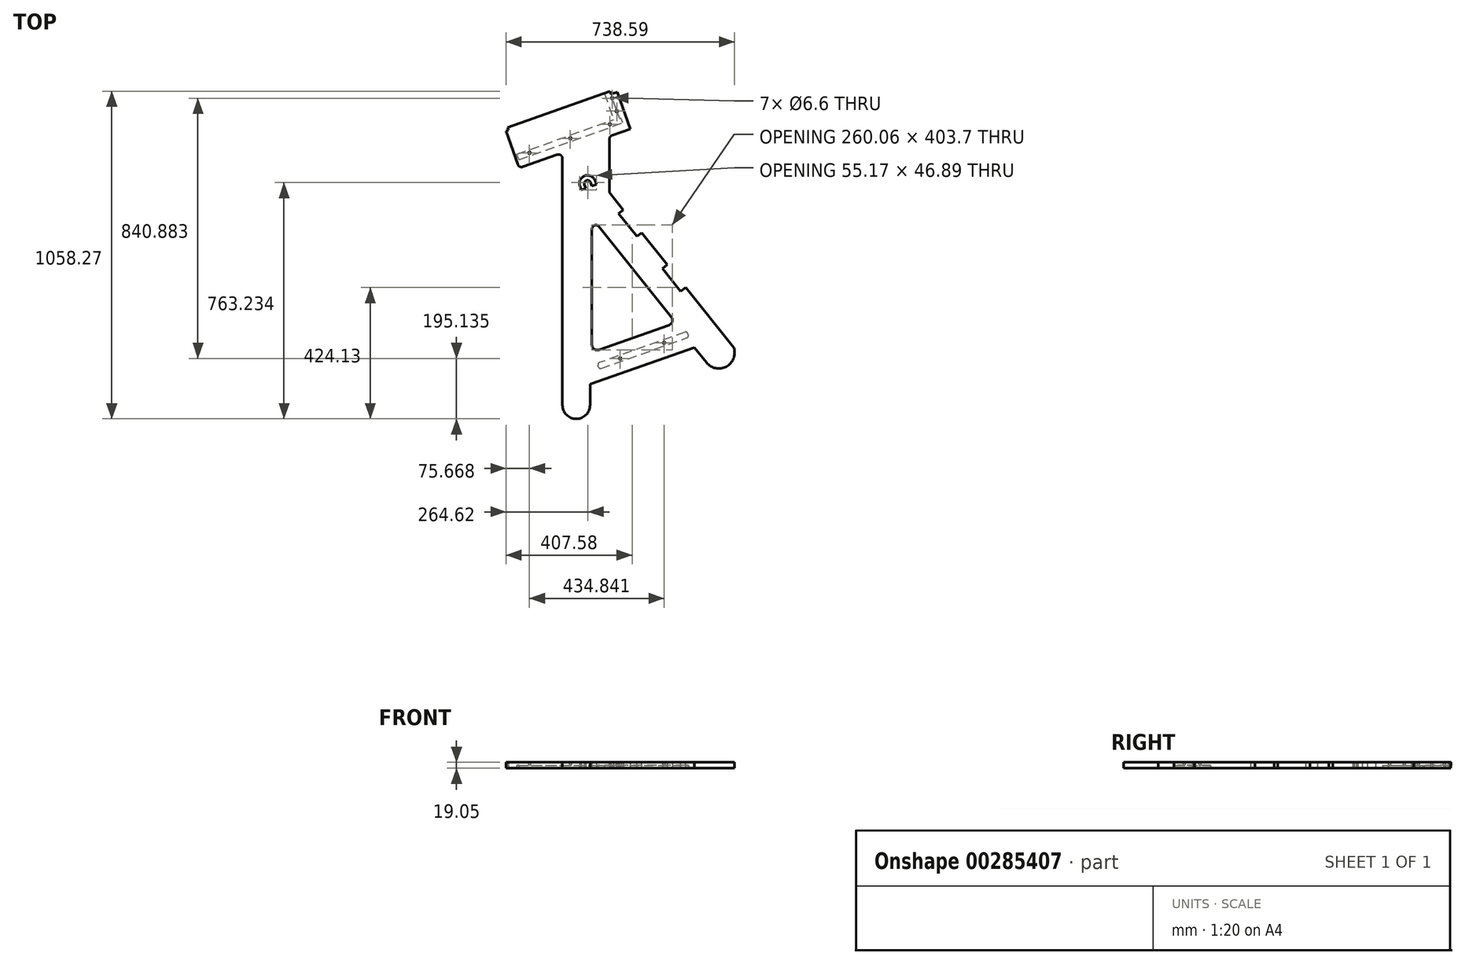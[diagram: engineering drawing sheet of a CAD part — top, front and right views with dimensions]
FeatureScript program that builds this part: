
annotation { "Feature Type Name" : "Feature", "Feature Type Description" : "" }
export const myFeature = defineFeature(function(context is Context, id is Id, definition is map)
    precondition{}
    {
        {
            var Q0;
            Q0=qCreatedBy(makeId("Top.planeOp"),FACE);
            var sketch = newSketch(context, id + "F0", { "sketchPlane" : qUnion([Q0])});
            skLineSegment(sketch, "E0", {"start": v(-306.62, -10.3) * mm, "end": v(-306.88, -10.27) * mm});
            skLineSegment(sketch, "E1", {"start": v(727.27, -289.32) * mm, "end": v(727.27, 507.63) * mm});
            skPoint(sketch, "E2.visualSharp", {"position": v(727.27, -334.1) * mm});
            skPoint(sketch, "E3.visualSharp", {"position": v(828.87, -334.66) * mm});
            skLineSegment(sketch, "E4", {"start": v(878.9, 569.94) * mm, "end": v(878.9, 402.04) * mm});
            skLineSegment(sketch, "E5", {"start": v(710.35, 519.6) * mm, "end": v(599.11, 480.45) * mm});
            skLineSegment(sketch, "E6", {"start": v(582.92, 488.22) * mm, "end": v(544.97, 596.03) * mm});
            skLineSegment(sketch, "E7", {"start": v(544.97, 596.03) * mm, "end": v(552.9, 598.83) * mm});
            skLineSegment(sketch, "E8", {"start": v(904.35, 722.53) * mm, "end": v(946.52, 602.74) * mm});
            skLineSegment(sketch, "E9", {"start": v(887.38, 581.92) * mm, "end": v(946.52, 602.74) * mm});
            skLineSegment(sketch, "E10", {"start": v(822.52, -95.2) * mm, "end": v(822.52, 279.38) * mm});
            skLineSegment(sketch, "E11", {"start": v(845.13, 287.31) * mm, "end": v(1078.98, -4.96) * mm});
            skPoint(sketch, "E12.visualSharp", {"position": v(822.52, 315.58) * mm});
            skArc(sketch, "E12.filletArc", {"start": v(845.13, 287.31) * mm, "mid": v(831.01, 291.36) * mm, "end": v(822.52, 279.38) * mm});
            skLineSegment(sketch, "E13", {"start": v(587.13, 476.24) * mm, "end": v(946.52, 602.74) * mm, "construction": true});
            skLineSegment(sketch, "E14", {"start": v(881.68, 394.1) * mm, "end": v(1281.26, -105.33) * mm});
            skArc(sketch, "E15", {"start": v(1192.97, -152.23) * mm, "mid": v(1256.56, -165.38) * mm, "end": v(1281.26, -105.33) * mm});
            skLineSegment(sketch, "E16", {"start": v(816.46, -289.32) * mm, "end": v(816.46, -221.63) * mm});
            skLineSegment(sketch, "E17", {"start": v(926.55, 733.52) * mm, "end": v(1268.68, -238.42) * mm, "construction": true});
            skPoint(sketch, "E18.visualSharp", {"position": v(878.9, 397.58) * mm});
            skArc(sketch, "E18.filletArc", {"start": v(878.9, 402.04) * mm, "mid": v(879.61, 397.83) * mm, "end": v(881.68, 394.1) * mm});
            skPoint(sketch, "E19.visualSharp", {"position": v(878.9, 578.94) * mm});
            skArc(sketch, "E19.filletArc", {"start": v(887.38, 581.92) * mm, "mid": v(881.23, 577.28) * mm, "end": v(878.9, 569.94) * mm});
            skArc(sketch, "E20.filletArc", {"start": v(727.27, 507.63) * mm, "mid": v(721.9, 518) * mm, "end": v(710.35, 519.6) * mm});
            skLineSegment(sketch, "E21", {"start": v(549.74, 607.81) * mm, "end": v(880.86, 724.36) * mm});
            skLineSegment(sketch, "E22", {"start": v(549.74, 607.81) * mm, "end": v(552.9, 598.83) * mm});
            skLineSegment(sketch, "E23", {"start": v(880.86, 724.36) * mm, "end": v(884.02, 715.38) * mm});
            skLineSegment(sketch, "E24.trimOffspring", {"start": v(884.02, 715.38) * mm, "end": v(904.35, 722.53) * mm, "construction": true});
            skLineSegment(sketch, "E25.trimOffspring", {"start": v(884.02, 715.38) * mm, "end": v(904.35, 722.53) * mm});
            skLineSegment(sketch, "E26", {"start": v(544.97, 596.03) * mm, "end": v(903.18, -421.63) * mm, "construction": true});
            skLineSegment(sketch, "E27", {"start": v(869.21, -325.12) * mm, "end": v(1232.7, -197.18) * mm, "construction": true});
            skLineSegment(sketch, "E28", {"start": v(816.46, -221.63) * mm, "end": v(1153.56, -102.97) * mm});
            skLineSegment(sketch, "E29", {"start": v(844.5, -110.78) * mm, "end": v(1071.57, -30.85) * mm});
            skArc(sketch, "E30", {"start": v(727.27, -289.32) * mm, "mid": v(771.86, -333.91) * mm, "end": v(816.46, -289.32) * mm});
            skPoint(sketch, "E31.visualSharp", {"position": v(587.13, 476.24) * mm});
            skArc(sketch, "E31.filletArc", {"start": v(582.92, 488.22) * mm, "mid": v(589.4, 480.98) * mm, "end": v(599.11, 480.45) * mm});
            skPoint(sketch, "E32.visualSharp", {"position": v(1093.5, -23.13) * mm});
            skArc(sketch, "E32.filletArc", {"start": v(1071.57, -30.85) * mm, "mid": v(1081.96, -19.82) * mm, "end": v(1078.98, -4.96) * mm});
            skPoint(sketch, "E33.visualSharp", {"position": v(822.52, -118.52) * mm});
            skArc(sketch, "E33.filletArc", {"start": v(822.52, -95.2) * mm, "mid": v(829.49, -108.68) * mm, "end": v(844.5, -110.78) * mm});
            skLineSegment(sketch, "E34", {"start": v(1153.56, -102.97) * mm, "end": v(1192.97, -152.23) * mm});
            skPoint(sketch, "E35", {"position": v(1256.56, -165.38) * mm});
            skPoint(sketch, "E36", {"position": v(771.86, -333.91) * mm});
            skPoint(sketch, "E37", {"position": v(1272.05, -152.68) * mm});
            skLineSegment(sketch, "E38", {"start": v(786.67, -331.38) * mm, "end": v(1249.58, -168.44) * mm, "construction": true});
            skArc(sketch, "E39", {"start": v(817.98, 430.01) * mm, "mid": v(804.77, 436.34) * mm, "end": v(798.43, 423.13) * mm});
            skArc(sketch, "E40", {"start": v(832.96, 435.28) * mm, "mid": v(799.5, 451.32) * mm, "end": v(783.46, 417.86) * mm});
            skLineSegment(sketch, "E41", {"start": v(783.46, 417.86) * mm, "end": v(787.67, 405.88) * mm});
            skLineSegment(sketch, "E42", {"start": v(787.67, 405.88) * mm, "end": v(802.65, 411.15) * mm});
            skLineSegment(sketch, "E43", {"start": v(802.65, 411.15) * mm, "end": v(798.43, 423.13) * mm});
            skLineSegment(sketch, "E44", {"start": v(817.98, 430.01) * mm, "end": v(822.2, 418.03) * mm});
            skLineSegment(sketch, "E45", {"start": v(822.2, 418.03) * mm, "end": v(837.17, 423.3) * mm});
            skLineSegment(sketch, "E46", {"start": v(837.17, 423.3) * mm, "end": v(832.96, 435.28) * mm});
            skSolve(sketch);
        }
        {
            var Q0;
            Q0=makeQuery(id+"F0.imprint","IMPRINT",FACE,{"disambiguationData":[TD([[makeQuery(id+"F0.imprint","IMPRINT",EDGE,{"derivedFrom":sQuery(id+"F0.wireOp",EDGE,"oAVC5DI8-kh1G-Qbfy-uwvq-Txyh6lFHP0Ui")}),1.0]])]});
            var Q1;
            Q1=makeQuery(id+"F0.imprint","IMPRINT",FACE,{"disambiguationData":[TD([[makeQuery(id+"F0.imprint","IMPRINT",EDGE,{"derivedFrom":sQuery(id+"F0.wireOp",EDGE,"E1")}),-1.0]])]});
            extrude(context, id + "F1", {"entities" : qUnion([Q0, Q1]), "depth" : 19.05 * mm});
        }
        {
            var Q0;
            {var subQ2=sQuery(id+"F0.wireOp",EDGE,"E1");Q0=makeQuery(id+"F0.imprint","IMPRINT",FACE,{"disambiguationData":[TD([[makeQuery(id+"F0.imprint","IMPRINT",EDGE,{"derivedFrom":subQ2}),-1.0]])]});}
            var sketch = newSketch(context, id + "F2", { "sketchPlane" : qUnion([Q0])});
            skLineSegment(sketch, "E47", {"start": v(852.3, -170.94) * mm, "end": v(1129.86, -72.11) * mm});
            skLineSegment(sketch, "E48", {"start": v(1123.5, -53.62) * mm, "end": v(845.93, -152.44) * mm});
            skLineSegment(sketch, "E49", {"start": v(1133.77, -64.18) * mm, "end": v(1131.67, -57.65) * mm});
            skLineSegment(sketch, "E50", {"start": v(844.12, -166.9) * mm, "end": v(842.02, -160.38) * mm});
            skPoint(sketch, "E51.visualSharp", {"position": v(846.13, -173.13) * mm});
            skArc(sketch, "E51.filletArc", {"start": v(844.12, -166.9) * mm, "mid": v(847.36, -170.65) * mm, "end": v(852.3, -170.94) * mm});
            skPoint(sketch, "E52.visualSharp", {"position": v(840.12, -154.51) * mm});
            skArc(sketch, "E52.filletArc", {"start": v(845.93, -152.44) * mm, "mid": v(842.36, -155.62) * mm, "end": v(842.02, -160.38) * mm});
            skPoint(sketch, "E53.visualSharp", {"position": v(1135.67, -70.04) * mm});
            skArc(sketch, "E53.filletArc", {"start": v(1129.86, -72.11) * mm, "mid": v(1133.43, -68.94) * mm, "end": v(1133.77, -64.18) * mm});
            skPoint(sketch, "E54.visualSharp", {"position": v(1129.66, -51.42) * mm});
            skArc(sketch, "E54.filletArc", {"start": v(1131.67, -57.65) * mm, "mid": v(1128.43, -53.9) * mm, "end": v(1123.5, -53.62) * mm});
            skSolve(sketch);
        }
        {
            var Q0;
            Q0=qSketchRegion(id+"F2",true);
            extrude(context, id + "F3", {"entities" : qUnion([Q0]), "operationType" : NewBodyOperationType.REMOVE, "depth" : 9.52 * mm});
        }
        {
            var Q0;
            {var subQ2=sQuery(id+"F0.wireOp",EDGE,"E1");Q0=makeQuery(id+"F0.imprint","IMPRINT",FACE,{"disambiguationData":[TD([[makeQuery(id+"F0.imprint","IMPRINT",EDGE,{"derivedFrom":subQ2}),-1.0]])]});}
            var sketch = newSketch(context, id + "F4", { "sketchPlane" : qUnion([Q0])});
            skLineSegment(sketch, "E55.bottom", {"start": v(586.5, 502.94) * mm, "end": v(921.88, 622.35) * mm});
            skLineSegment(sketch, "E55.top", {"start": v(579.94, 521.37) * mm, "end": v(892.72, 632.73) * mm});
            skLineSegment(sketch, "E55.left", {"start": v(586.5, 502.94) * mm, "end": v(579.94, 521.37) * mm});
            skLineSegment(sketch, "E56", {"start": v(862.38, 717.95) * mm, "end": v(892.72, 632.73) * mm});
            skPoint(sketch, "E57.0", {"position": v(884.02, 715.38) * mm});
            skPoint(sketch, "E58.0", {"position": v(880.86, 724.36) * mm});
            skLineSegment(sketch, "E59", {"start": v(880.86, 724.36) * mm, "end": v(884.02, 715.38) * mm});
            skLineSegment(sketch, "E60", {"start": v(880.86, 724.36) * mm, "end": v(862.38, 717.95) * mm});
            skLineSegment(sketch, "E61", {"start": v(912.13, 636.43) * mm, "end": v(884.02, 715.38) * mm});
            skLineSegment(sketch, "E62", {"start": v(912.13, 636.43) * mm, "end": v(916.33, 637.93) * mm});
            skLineSegment(sketch, "E63", {"start": v(921.88, 622.35) * mm, "end": v(916.33, 637.93) * mm});
            skSolve(sketch);
        }
        {
            var Q0;
            Q0=qSketchRegion(id+"F4",true);
            extrude(context, id + "F5", {"entities" : qUnion([Q0]), "operationType" : NewBodyOperationType.REMOVE, "depth" : 9.52 * mm});
        }
        {
            var Q0;
            Q0=makeQuery(id+"F1.opExtrude","SWEPT_FACE",FACE,{"disambiguationData":[OSD([sQuery(id+"F0.wireOp",EDGE,"E14")])]});
            var sketch = newSketch(context, id + "F6", { "sketchPlane" : qUnion([Q0])});
            skLineSegment(sketch, "E64", {"start": v(-310.5, 19.05) * mm, "end": v(-310.5, 0) * mm});
            skLineSegment(sketch, "E65", {"start": v(-310.5, 0) * mm, "end": v(-405.25, 0) * mm});
            skLineSegment(sketch, "E66", {"start": v(-405.25, 0) * mm, "end": v(-405.25, 19.05) * mm});
            skLineSegment(sketch, "E67", {"start": v(-405.25, 19.05) * mm, "end": v(-310.5, 19.05) * mm});
            skLineSegment(sketch, "E68", {"start": v(-537.62, 21.33) * mm, "end": v(-537.62, -0.7) * mm});
            skLineSegment(sketch, "E69", {"start": v(-537.62, -0.7) * mm, "end": v(-632.36, -0.7) * mm});
            skLineSegment(sketch, "E70", {"start": v(-632.36, -0.7) * mm, "end": v(-632.36, 21.33) * mm});
            skLineSegment(sketch, "E71", {"start": v(-632.36, 21.33) * mm, "end": v(-537.62, 21.33) * mm});
            skSolve(sketch);
        }
        {
            var Q0;
            Q0=qSketchRegion(id+"F6",true);
            extrude(context, id + "F7", {"entities" : qUnion([Q0]), "operationType" : NewBodyOperationType.REMOVE, "oppositeDirection" : true, "depth" : 19.56 * mm});
        }
        {
            var Q0;
            Q0=makeQuery(id+"F0.imprint","IMPRINT",FACE,{"disambiguationData":[TD([[makeQuery(id+"F0.imprint","IMPRINT",EDGE,{"derivedFrom":sQuery(id+"F0.wireOp",EDGE,"E1")}),-1.0]])]});
            var sketch = newSketch(context, id + "F8", { "sketchPlane" : qUnion([Q0])});
            skLineSegment(sketch, "E72", {"start": v(916.91, 620.58) * mm, "end": v(879.28, 726.3) * mm, "construction": true});
            skLineSegment(sketch, "E73.0", {"start": v(912.13, 636.43) * mm, "end": v(884.02, 715.38) * mm});
            skCircle(sketch, "E74", {"center": v(902.66, 660.61) * mm, "radius": 3.3 * mm});
            skCircle(sketch, "E75", {"center": v(887.92, 702.1) * mm, "radius": 3.3 * mm});
            skLineSegment(sketch, "E76", {"start": v(921.57, 632.52) * mm, "end": v(583.89, 512.3) * mm, "construction": true});
            skCircle(sketch, "E77", {"center": v(880.54, 617.91) * mm, "radius": 3.3 * mm});
            skCircle(sketch, "E78", {"center": v(620.64, 525.38) * mm, "radius": 3.3 * mm});
            skCircle(sketch, "E79", {"center": v(752.73, 572.4) * mm, "radius": 3.3 * mm});
            skLineSegment(sketch, "E80.0", {"start": v(1133.77, -64.18) * mm, "end": v(1131.67, -57.65) * mm});
            skLineSegment(sketch, "E81.0", {"start": v(1123.5, -53.62) * mm, "end": v(845.93, -152.44) * mm});
            skLineSegment(sketch, "E82", {"start": v(1123.33, -64.1) * mm, "end": v(843.4, -163.77) * mm, "construction": true});
            skCircle(sketch, "E83", {"center": v(1055.48, -88.26) * mm, "radius": 3.3 * mm});
            skCircle(sketch, "E84", {"center": v(913.6, -138.78) * mm, "radius": 3.3 * mm});
            skLineSegment(sketch, "E85", {"start": v(752.73, 572.4) * mm, "end": v(620.64, 525.38) * mm});
            skSolve(sketch);
        }
        {
            var Q0;
            Q0=qSketchRegion(id+"F8",true);
            extrude(context, id + "F9", {"entities" : qUnion([Q0]), "operationType" : NewBodyOperationType.REMOVE, "endBound" : BoundingType.THROUGH_ALL, "depth" : 25.4 * mm});
        }
        {
            var Q0;
            Q0=sQuery(id+"F0.wireOp",EDGE,"E40");
            var Q1;
            Q1=sQuery(id+"F0.wireOp",EDGE,"E46");
            var Q2;
            Q2=sQuery(id+"F0.wireOp",EDGE,"E39");
            var Q3;
            Q3=sQuery(id+"F0.wireOp",EDGE,"E44");
            var Q4;
            Q4=sQuery(id+"F0.wireOp",EDGE,"E45");
            var Q5;
            Q5=sQuery(id+"F0.wireOp",EDGE,"E43");
            var Q6;
            Q6=sQuery(id+"F0.wireOp",EDGE,"E41");
            var Q7;
            Q7=sQuery(id+"F0.wireOp",EDGE,"E42");
            extrude(context, id + "F10", {"bodyType" : ToolBodyType.SURFACE, "surfaceEntities" : qUnion([Q0, Q1, Q2, Q3, Q4, Q5, Q6, Q7]), "depth" : 25.4 * mm});
        }
    });
